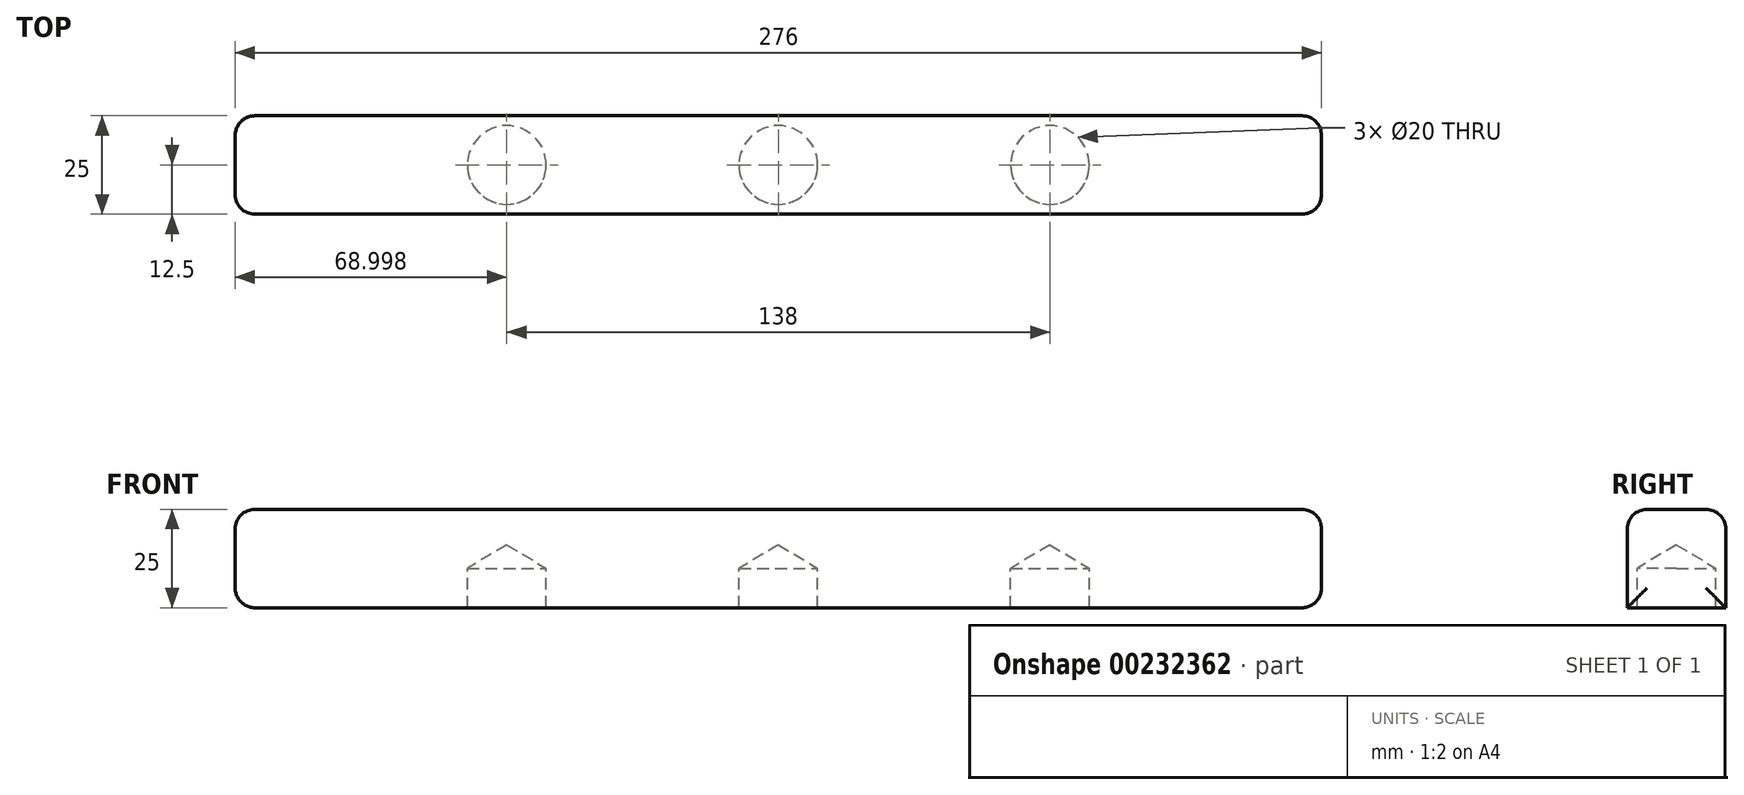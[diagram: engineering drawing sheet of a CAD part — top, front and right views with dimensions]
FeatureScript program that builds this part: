
annotation { "Feature Type Name" : "Feature", "Feature Type Description" : "" }
export const myFeature = defineFeature(function(context is Context, id is Id, definition is map)
    precondition{}
    {
        {
            var Q0;
            Q0=qCreatedBy(makeId("Front.planeOp"),FACE);
            var sketch = newSketch(context, id + "F0", { "sketchPlane" : qUnion([Q0])});
            skLineSegment(sketch, "E0.bottom", {"start": v(-66.73, 25) * mm, "end": v(209.27, 25) * mm});
            skLineSegment(sketch, "E0.top", {"start": v(-66.73, 0) * mm, "end": v(209.27, 0) * mm});
            skLineSegment(sketch, "E0.left", {"start": v(-66.73, 25) * mm, "end": v(-66.73, 0) * mm});
            skLineSegment(sketch, "E0.right", {"start": v(209.27, 25) * mm, "end": v(209.27, 0) * mm});
            skSolve(sketch);
        }
        {
            var Q0;
            Q0 = qSketchRegion(id + "F0", true);
            extrude(context, id + "F1", {"entities" : qUnion([Q0]), "depth" : 25 * mm});
        }
        {
            var Q0;
            Q0=qCreatedBy(makeId("Top.planeOp"),FACE);
            var sketch = newSketch(context, id + "F2", { "sketchPlane" : qUnion([Q0])});
            skCircle(sketch, "E1", {"center": v(71.27, -12.5) * mm, "radius": 10 * mm});
            skCircle(sketch, "E2.1.0.0", {"center": v(140.27, -12.5) * mm, "radius": 10 * mm});
            skLineSegment(sketch, "E2.direction1", {"start": v(71.27, -12.5) * mm, "end": v(140.27, -12.5) * mm, "construction": true});
            skCircle(sketch, "E3.1.0.0", {"center": v(2.27, -12.5) * mm, "radius": 10 * mm});
            skLineSegment(sketch, "E3.direction1", {"start": v(71.27, -12.5) * mm, "end": v(2.27, -12.5) * mm, "construction": true});
            skSolve(sketch);
        }
        {
            var Q0;
            Q0=sQuery(id+"F2.wireOp",VERTEX,"E2.direction1.end");
            var Q1;
            Q1=sQuery(id+"F2.wireOp",VERTEX,"E1.center");
            var Q2;
            Q2=sQuery(id+"F2.wireOp",VERTEX,"E3.direction1.end");
            var Q3;
            Q3=makeQuery(id+"F1.opExtrude","SWEPT_BODY",BODY,{"disambiguationData":[OSD([sQuery(id+"F0.wireOp",EDGE,"E0.bottom"),sQuery(id+"F0.wireOp",EDGE,"E0.top"),sQuery(id+"F0.wireOp",EDGE,"E0.left"),sQuery(id+"F0.wireOp",EDGE,"E0.right")])]});
            hole(context, id + "F3", {"style" : HoleStyle.SIMPLE, "endStyle" : HoleEndStyle.BLIND, "oppositeDirection" : true, "holeDiameter" : 20 * mm, "holeDepth" : 10 * mm, "locations" : qUnion([Q0, Q1, Q2]), "scope" : qUnion([Q3]), "startStyle" : HoleStartStyle.SKETCH});
        }
        {
            var Q0;
            Q0=makeQuery(id+"F1.opExtrude","SWEPT_FACE",FACE,{"disambiguationData":[OSD([sQuery(id+"F0.wireOp",EDGE,"E0.bottom")])]});
            var Q1;
            Q1=makeQuery(id+"F1.opExtrude","SWEPT_FACE",FACE,{"disambiguationData":[OSD([sQuery(id+"F0.wireOp",EDGE,"E0.right")])]});
            var Q2;
            Q2=makeQuery(id+"F1.opExtrude","SWEPT_FACE",FACE,{"disambiguationData":[OSD([sQuery(id+"F0.wireOp",EDGE,"E0.left")])]});
            fillet(context, id + "F4", {"entities" : qUnion([Q0, Q1, Q2]), "radius" : 5 * mm, "tangentPropagation" : true, "allowEdgeOverflow" : false});
        }
    });
